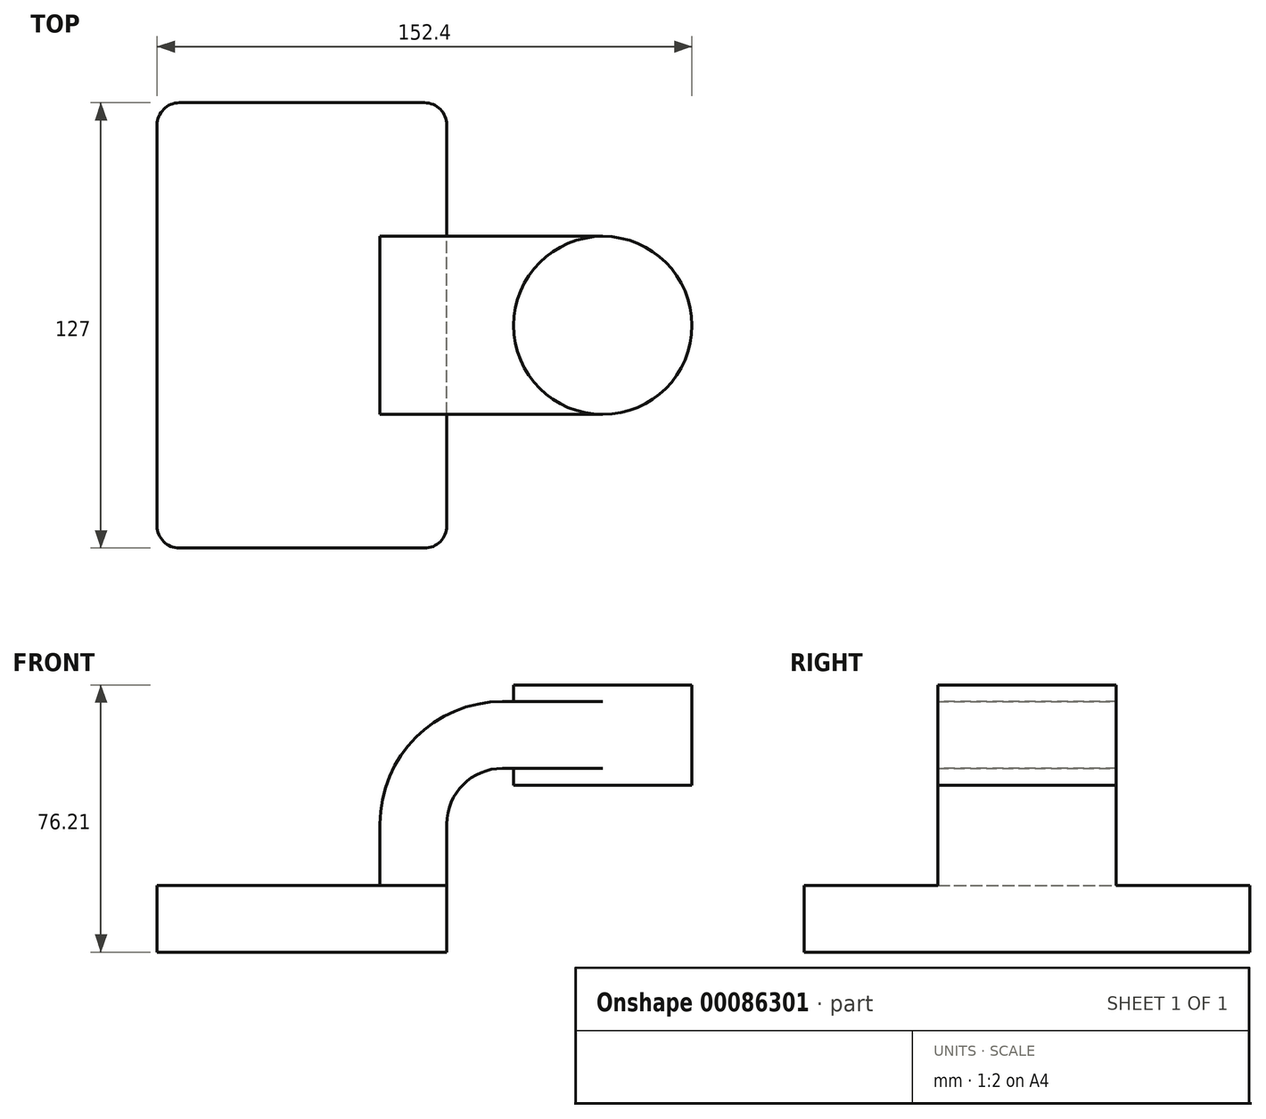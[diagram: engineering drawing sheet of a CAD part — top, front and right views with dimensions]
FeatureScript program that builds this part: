
annotation { "Feature Type Name" : "Feature", "Feature Type Description" : "" }
export const myFeature = defineFeature(function(context is Context, id is Id, definition is map)
    precondition{}
    {
        {
            var Q0;
            Q0=qCreatedBy(makeId("Front.planeOp"),FACE);
            var sketch = newSketch(context, id + "F0", { "sketchPlane" : qUnion([Q0])});
            skLineSegment(sketch, "E0.bottom", {"start": v(41.28, -9.52) * mm, "end": v(-41.27, -9.52) * mm});
            skLineSegment(sketch, "E0.top", {"start": v(41.27, 9.53) * mm, "end": v(-41.28, 9.53) * mm});
            skLineSegment(sketch, "E0.left", {"start": v(41.28, -9.52) * mm, "end": v(41.28, 9.53) * mm});
            skLineSegment(sketch, "E0.right", {"start": v(-41.27, -9.52) * mm, "end": v(-41.28, 9.53) * mm});
            skPoint(sketch, "E0.middle", {"position": v(0, 0) * mm});
            skLineSegment(sketch, "E1.bottom", {"start": v(111.12, 38.1) * mm, "end": v(60.32, 38.1) * mm});
            skLineSegment(sketch, "E1.top", {"start": v(111.12, 66.68) * mm, "end": v(60.32, 66.68) * mm});
            skLineSegment(sketch, "E1.left", {"start": v(111.12, 38.1) * mm, "end": v(111.12, 66.68) * mm});
            skLineSegment(sketch, "E1.right", {"start": v(60.32, 38.1) * mm, "end": v(60.32, 66.68) * mm});
            skPoint(sketch, "E1.middle", {"position": v(85.72, 52.39) * mm});
            skLineSegment(sketch, "E2", {"start": v(41.27, 9.53) * mm, "end": v(41.27, 27) * mm});
            skArc(sketch, "E3", {"start": v(41.27, 27) * mm, "mid": v(45.92, 38.23) * mm, "end": v(57.15, 42.88) * mm});
            skLineSegment(sketch, "E4", {"start": v(57.15, 42.88) * mm, "end": v(85.72, 42.88) * mm});
            skLineSegment(sketch, "E5.0", {"start": v(57.15, 61.93) * mm, "end": v(85.72, 61.93) * mm});
            skArc(sketch, "E5.1", {"start": v(22.23, 27) * mm, "mid": v(32.45, 51.7) * mm, "end": v(57.15, 61.93) * mm});
            skLineSegment(sketch, "E5.2", {"start": v(22.23, 9.53) * mm, "end": v(22.23, 27) * mm});
            skLineSegment(sketch, "E6", {"start": v(85.72, 66.68) * mm, "end": v(85.72, 38.1) * mm});
            skFitSpline(sketch, "E7", {"points": [v(-41.28, 9.53) * mm, v(57.15, 61.93) * mm], "startDerivative": vector(2.14, 115.52) * mm, "endDerivative": vector(107.7, -4.2) * mm});
            skSolve(sketch);
        }
        {
            var Q0;
            Q0=makeQuery(id+"F0.imprint","IMPRINT",FACE,{"disambiguationData":[TD([[makeQuery(id+"F0.imprint","IMPRINT",EDGE,{"derivedFrom":sQuery(id+"F0.wireOp",EDGE,"E0.bottom")}),-1.0]])]});
            extrude(context, id + "F1", {"entities" : qUnion([Q0]), "endBound" : BoundingType.SYMMETRIC, "depth" : 127 * mm});
        }
        {
            var Q0;
            {var subQ1=sQuery(id+"F0.wireOp",EDGE,"E2");Q0=makeQuery(id+"F0.imprint","IMPRINT",FACE,{"disambiguationData":[TD([[makeQuery(id+"F0.imprint","IMPRINT",EDGE,{"derivedFrom":subQ1}),1.0]])]});}
            var Q1;
            {var subQ0=sQuery(id+"F0.wireOp",EDGE,"E4");var subQ1=sQuery(id+"F0.wireOp",EDGE,"E1.right");var subQ2=makeQuery(id+"F0.imprint","INTERSECT",VERTEX,{"derivedFrom":[subQ1,subQ0]});Q1=makeQuery(id+"F0.imprint","IMPRINT",FACE,{"disambiguationData":[TD([[makeQuery(id+"F0.imprint","IMPRINT",EDGE,{"disambiguationData":[TD([[subQ2,-1.0]])],"derivedFrom":subQ1}),-1.0]])]});}
            extrude(context, id + "F2", {"entities" : qUnion([Q0, Q1]), "operationType" : NewBodyOperationType.ADD, "endBound" : BoundingType.SYMMETRIC, "depth" : 50.8 * mm});
        }
        {
            var Q0;
            Q0=makeQuery(id+"F0.imprint","IMPRINT",FACE,{"disambiguationData":[TD([[makeQuery(id+"F0.imprint","IMPRINT",EDGE,{"derivedFrom":sQuery(id+"F0.wireOp",EDGE,"E5.1")}),1.0]])]});
            extrude(context, id + "F3", {"entities" : qUnion([Q0]), "operationType" : NewBodyOperationType.ADD, "endBound" : BoundingType.SYMMETRIC, "depth" : 15.88 * mm});
        }
        {
            var Q0;
            {var subQ0=sQuery(id+"F0.wireOp",EDGE,"E1.left");Q0=makeQuery(id+"F0.imprint","IMPRINT",FACE,{"disambiguationData":[TD([[makeQuery(id+"F0.imprint","IMPRINT",EDGE,{"derivedFrom":subQ0}),1.0]])]});}
            var Q1;
            Q1=sQuery(id+"F0.wireOp",EDGE,"E6");
            revolve(context, id + "F4", {"operationType" : NewBodyOperationType.ADD, "entities" : qUnion([Q0]), "axis" : qUnion([Q1]), "revolveType" : RevolveType.FULL});
        }
        {
            var Q0;
            Q0=makeQuery(id+"F1.opExtrude","CAP_EDGE",EDGE,{"disambiguationData":[OSD([sQuery(id+"F0.wireOp",EDGE,"E0.left")])],"isStart":false});
            var Q1;
            Q1=makeQuery(id+"F1.opExtrude","CAP_EDGE",EDGE,{"disambiguationData":[OSD([sQuery(id+"F0.wireOp",EDGE,"E0.right")])],"isStart":false});
            var Q2;
            Q2=makeQuery(id+"F1.opExtrude","CAP_EDGE",EDGE,{"disambiguationData":[OSD([sQuery(id+"F0.wireOp",EDGE,"E0.left")])],"isStart":true});
            var Q3;
            Q3=makeQuery(id+"F1.opExtrude","CAP_EDGE",EDGE,{"disambiguationData":[OSD([sQuery(id+"F0.wireOp",EDGE,"E0.right")])],"isStart":true});
            fillet(context, id + "F5", {"entities" : qUnion([Q0, Q1, Q2, Q3]), "radius" : 6.35 * mm, "tangentPropagation" : true, "allowEdgeOverflow" : false});
        }
    });
